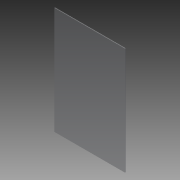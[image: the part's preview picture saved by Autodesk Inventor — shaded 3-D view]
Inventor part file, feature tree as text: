
AUTODESK INVENTOR PART (.ipt)
format: ipt  version: 2014 (Build 180170000, 170)  size: 71,168 bytes
history: native  units: in
note: dims shown in document units (in); Inventor stores cm internally (conversion verified against a paired STEP export)
features: extrude x1, sketch x1
ambient origin geometry x8: Origin, YZ Plane, XZ Plane, XY Plane, X Axis, Y Axis, Z Axis, Center Point
bodies: Solid1 (feature_tree)
feature tree (2):
  extrude  "Extrusion1"  Depth=5.91in
  sketch  "Sketch1"  dims[d2=0.0625in d3=0.0in d8=5.91in d28=9.0in]
